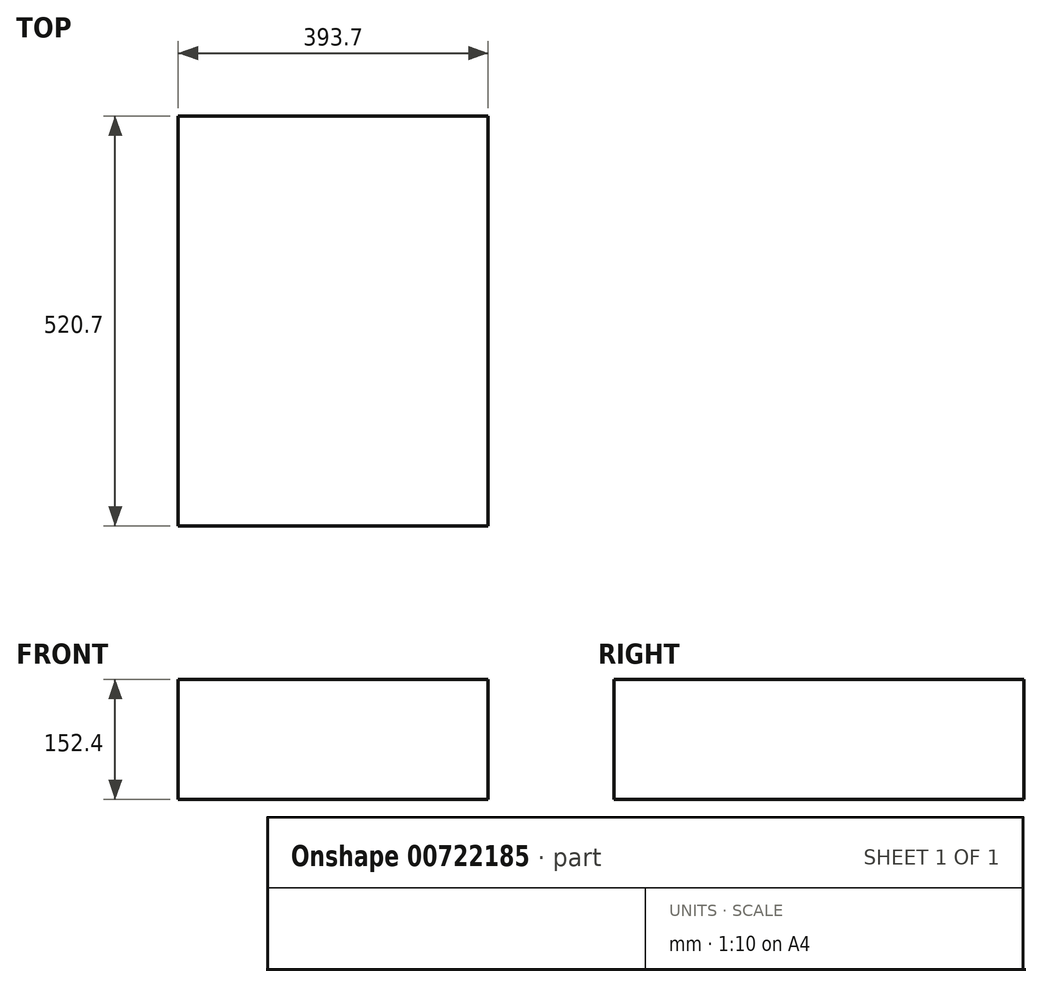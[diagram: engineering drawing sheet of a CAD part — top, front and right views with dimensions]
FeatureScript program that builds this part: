
annotation { "Feature Type Name" : "Feature", "Feature Type Description" : "" }
export const myFeature = defineFeature(function(context is Context, id is Id, definition is map)
    precondition{}
    {
        {
            var Q0;
            Q0=qCreatedBy(makeId("Top.planeOp"),FACE);
            var sketch = newSketch(context, id + "F0", { "sketchPlane" : qUnion([Q0])});
            skLineSegment(sketch, "E0.bottom", {"start": v(-196.85, 0) * mm, "end": v(196.85, 0) * mm});
            skLineSegment(sketch, "E0.top", {"start": v(-196.85, 520.7) * mm, "end": v(196.85, 520.7) * mm});
            skLineSegment(sketch, "E0.left", {"start": v(-196.85, 0) * mm, "end": v(-196.85, 520.7) * mm});
            skLineSegment(sketch, "E0.right", {"start": v(196.85, 0) * mm, "end": v(196.85, 520.7) * mm});
            skLineSegment(sketch, "E1", {"start": v(0, 0) * mm, "end": v(0, 397.98) * mm, "construction": true});
            skSolve(sketch);
        }
        {
            var Q0;
            Q0=qSketchRegion(id+"F0",true);
            extrude(context, id + "F1", {"entities" : qUnion([Q0]), "depth" : 152.4 * mm, "offsetDistance" : 25.4 * mm});
        }
    });
